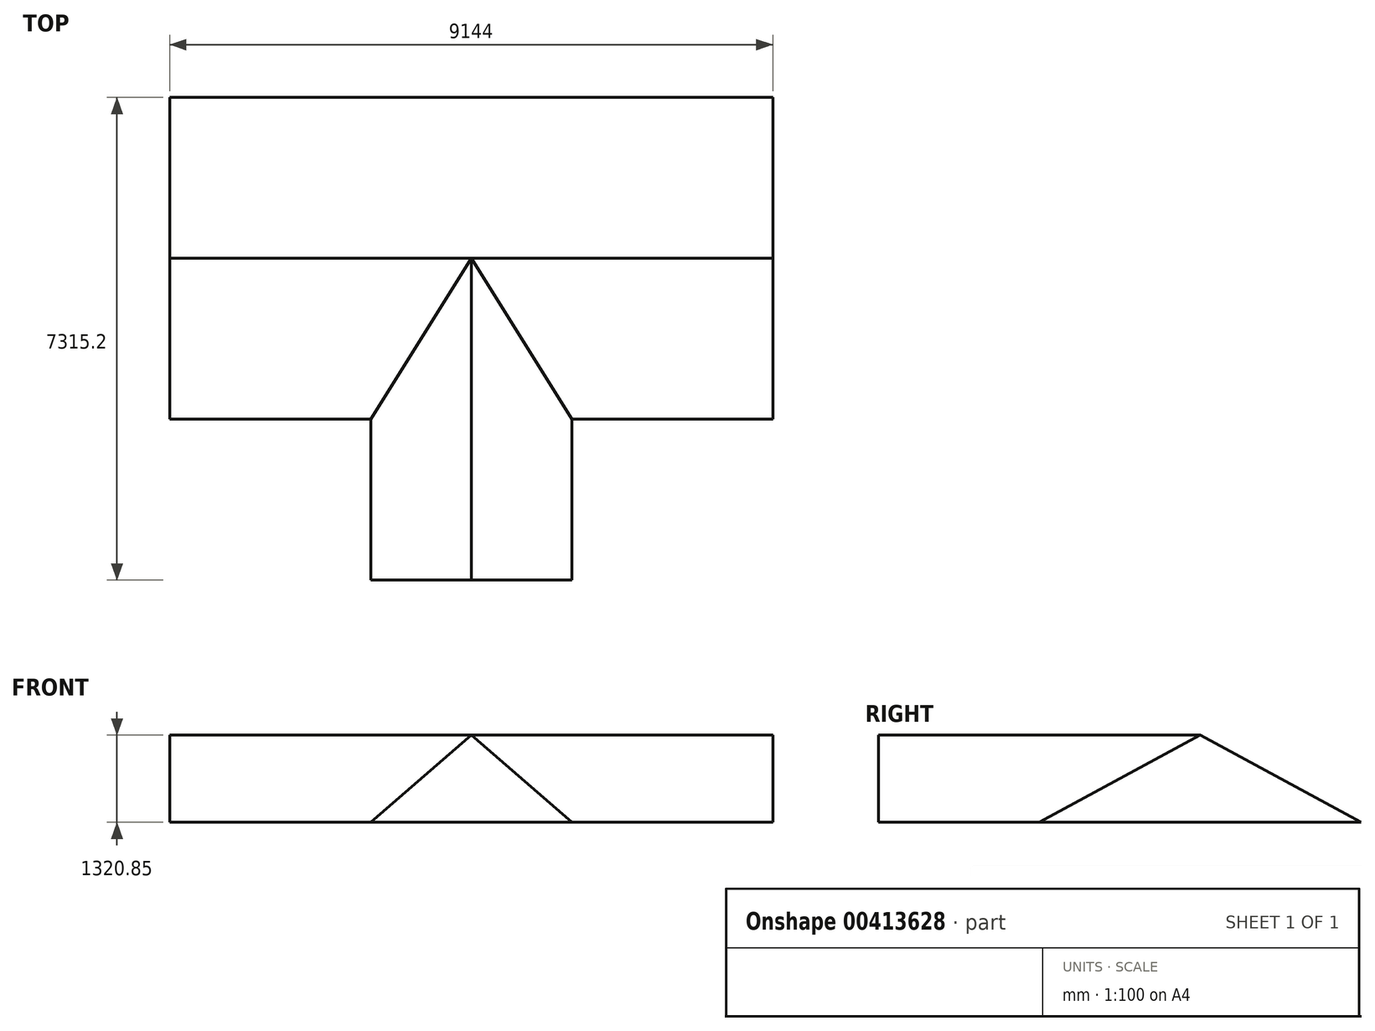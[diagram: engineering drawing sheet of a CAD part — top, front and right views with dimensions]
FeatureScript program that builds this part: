
annotation { "Feature Type Name" : "Feature", "Feature Type Description" : "" }
export const myFeature = defineFeature(function(context is Context, id is Id, definition is map)
    precondition{}
    {
        {
            var Q0;
            Q0=qCreatedBy(makeId("Right.planeOp"),FACE);
            var sketch = newSketch(context, id + "F0", { "sketchPlane" : qUnion([Q0])});
            skLineSegment(sketch, "E0.bottom", {"start": v(2438.4, -1320.85) * mm, "end": v(-2438.4, -1320.85) * mm});
            skPoint(sketch, "E0.middle", {"position": v(0, 0) * mm});
            skLineSegment(sketch, "E1", {"start": v(-2438.4, -1320.85) * mm, "end": v(0, 0) * mm});
            skLineSegment(sketch, "E2", {"start": v(0, 0) * mm, "end": v(2438.4, -1320.85) * mm});
            skSolve(sketch);
        }
        {
            var Q0;
            Q0=qCreatedBy(makeId("Front.planeOp"),FACE);
            var sketch = newSketch(context, id + "F1", { "sketchPlane" : qUnion([Q0])});
            skPoint(sketch, "E3.0", {"position": v(0, -660.42) * mm});
            skLineSegment(sketch, "E4.top", {"start": v(1524, -1320.85) * mm, "end": v(-1524, -1320.85) * mm});
            skLineSegment(sketch, "E5", {"start": v(0, 0) * mm, "end": v(-1524, -1320.85) * mm});
            skLineSegment(sketch, "E6", {"start": v(0, 0) * mm, "end": v(1524, -1320.85) * mm});
            skSolve(sketch);
        }
        {
            var Q0;
            Q0 = qSketchRegion(id + "F1", true);
            extrude(context, id + "F2", {"entities" : qUnion([Q0]), "depth" : 4876.8 * mm, "offsetDistance" : 30.48 * mm});
        }
        {
            var Q0;
            Q0=makeQuery(id+"F0.imprint","IMPRINT",FACE,{"disambiguationData":[TD([[makeQuery(id+"F0.imprint","IMPRINT",EDGE,{"derivedFrom":sQuery(id+"F0.wireOp",EDGE,"E0.bottom")}),-1.0]])]});
            extrude(context, id + "F3", {"entities" : qUnion([Q0]), "operationType" : NewBodyOperationType.ADD, "endBound" : BoundingType.SYMMETRIC, "depth" : 9144 * mm, "offsetDistance" : 30.48 * mm});
        }
    });
